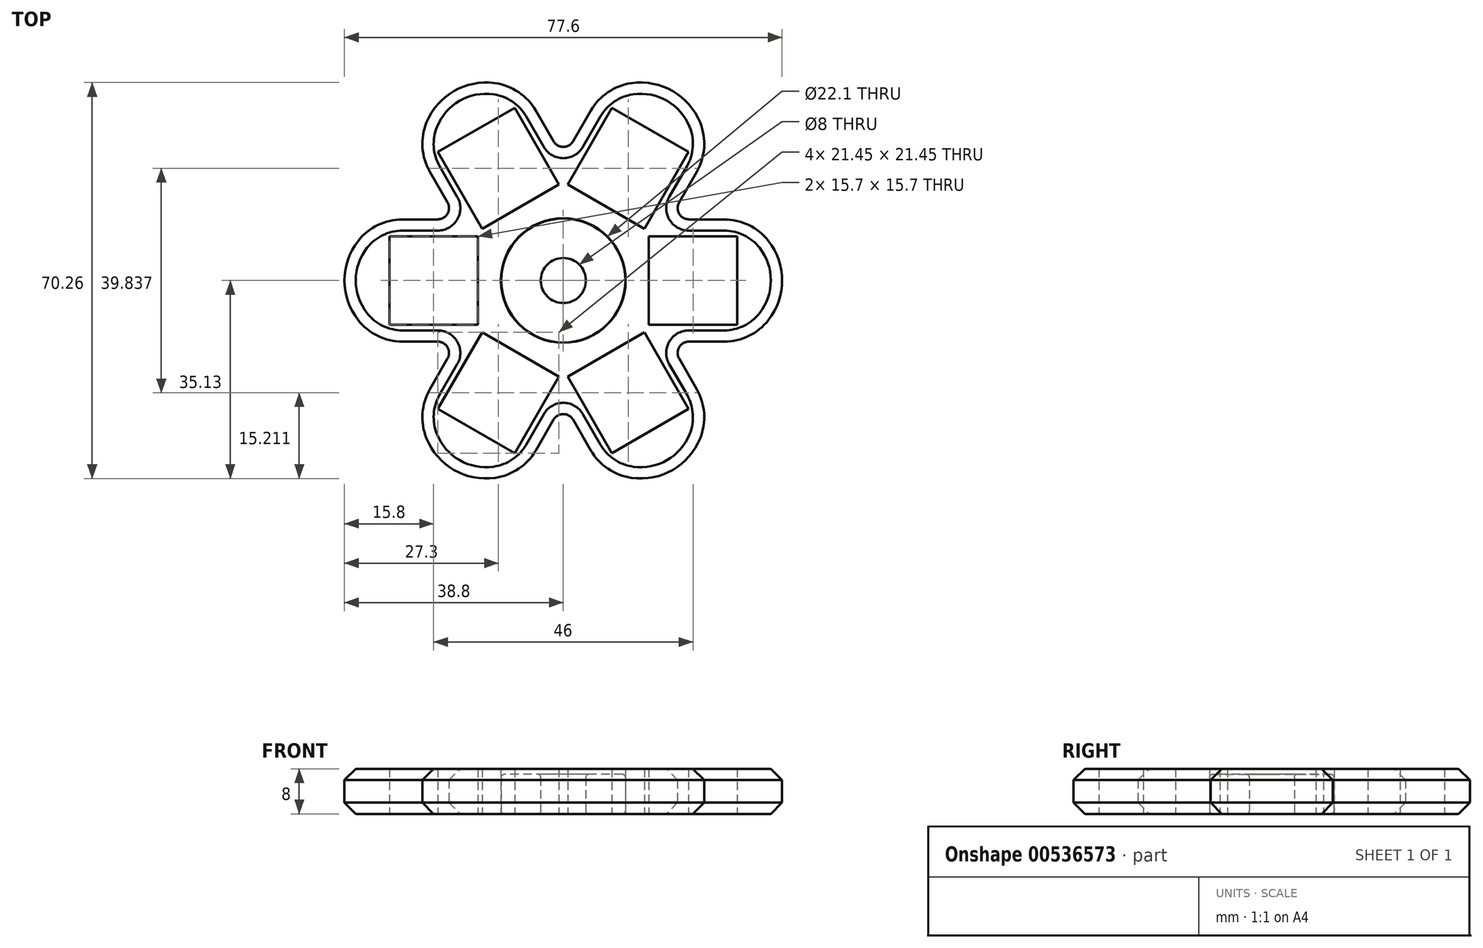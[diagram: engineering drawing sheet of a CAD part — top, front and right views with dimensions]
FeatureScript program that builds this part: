
annotation { "Feature Type Name" : "Feature", "Feature Type Description" : "" }
export const myFeature = defineFeature(function(context is Context, id is Id, definition is map)
    precondition{}
    {
        {
            var Q0;
            Q0=qCreatedBy(makeId("Top.planeOp"),FACE);
            var sketch = newSketch(context, id + "F0", { "sketchPlane" : qUnion([Q0])});
            skCircle(sketch, "E0", {"center": v(0, 0) * mm, "radius": 11 * mm});
            skCircle(sketch, "E1", {"center": v(0, 0) * mm, "radius": 4 * mm});
            skSolve(sketch);
        }
        {
            var Q0;
            Q0=makeQuery(id+"F0.imprint","IMPRINT",FACE,{"disambiguationData":[TD([[makeQuery(id+"F0.imprint","IMPRINT",EDGE,{"derivedFrom":sQuery(id+"F0.wireOp",EDGE,"E0")}),1.0]])]});
            extrude(context, id + "F1", {"entities" : qUnion([Q0]), "depth" : 7 * mm, "offsetDistance" : 25 * mm});
        }
        {
            var Q0;
            Q0=makeQuery(id+"F1.opExtrude","CAP_FACE",FACE,{"disambiguationData":[OSD([sQuery(id+"F0.wireOp",EDGE,"E0"),sQuery(id+"F0.wireOp",EDGE,"E1")])],"isStart":true});
            var sketch = newSketch(context, id + "F2", { "sketchPlane" : qUnion([Q0])});
            skCircle(sketch, "E2.0", {"center": v(0, 0) * mm, "radius": 11.05 * mm});
            skCircle(sketch, "E3.0", {"center": v(0, 0) * mm, "radius": 15.05 * mm});
            skLineSegment(sketch, "E4", {"start": v(0, 0) * mm, "end": v(-23, 0) * mm, "construction": true});
            skLineSegment(sketch, "E5.bottom", {"start": v(-30.85, -7.85) * mm, "end": v(-15.15, -7.85) * mm});
            skLineSegment(sketch, "E5.top", {"start": v(-30.85, 7.85) * mm, "end": v(-15.15, 7.85) * mm});
            skLineSegment(sketch, "E5.left", {"start": v(-30.85, -7.85) * mm, "end": v(-30.85, 7.85) * mm});
            skLineSegment(sketch, "E5.right", {"start": v(-15.15, -7.85) * mm, "end": v(-15.15, 7.85) * mm});
            skPoint(sketch, "E5.middle", {"position": v(-23, 0) * mm});
            skCircle(sketch, "E6", {"center": v(0, 0) * mm, "radius": 50 * mm, "construction": true});
            skLineSegment(sketch, "E7", {"start": v(-23, 0) * mm, "end": v(-38.8, 0) * mm, "construction": true});
            skLineSegment(sketch, "E8", {"start": v(-30.85, 7.85) * mm, "end": v(-30.85, 10.85) * mm, "construction": true});
            skLineSegment(sketch, "E9.0", {"start": v(-23, 10.85) * mm, "end": v(-30.85, 10.85) * mm});
            skLineSegment(sketch, "E9.1", {"start": v(0, 10.85) * mm, "end": v(-2.1, 10.85) * mm, "construction": true});
            skLineSegment(sketch, "E10.trimOffspring", {"start": v(-10.43, 10.85) * mm, "end": v(-23, 10.85) * mm});
            skLineSegment(sketch, "E11.MirrorCS", {"start": v(-10.43, -10.85) * mm, "end": v(-23, -10.85) * mm});
            skLineSegment(sketch, "E12.MirrorCS", {"start": v(-23, -10.85) * mm, "end": v(-30.85, -10.85) * mm});
            skArc(sketch, "E13", {"start": v(-30.85, 10.85) * mm, "mid": v(-38.8, 0) * mm, "end": v(-30.85, -10.85) * mm});
            skLineSegment(sketch, "E14.1.0", {"start": v(-8.63, -30.64) * mm, "end": v(-0.78, -17.05) * mm});
            skLineSegment(sketch, "E14.1.1", {"start": v(-0.78, -17.05) * mm, "end": v(-14.37, -9.2) * mm});
            skLineSegment(sketch, "E14.1.2", {"start": v(-22.22, -22.8) * mm, "end": v(-14.37, -9.2) * mm});
            skLineSegment(sketch, "E14.1.3", {"start": v(-14.61, -3.6) * mm, "end": v(-20.9, -14.5) * mm});
            skLineSegment(sketch, "E14.1.4", {"start": v(-20.9, -14.5) * mm, "end": v(-24.82, -21.3) * mm});
            skLineSegment(sketch, "E14.1.5", {"start": v(-8.63, -30.64) * mm, "end": v(-22.22, -22.8) * mm});
            skArc(sketch, "E14.1.6", {"start": v(-24.82, -21.3) * mm, "mid": v(-19.4, -33.6) * mm, "end": v(-6.03, -32.14) * mm});
            skLineSegment(sketch, "E14.1.7", {"start": v(-2.1, -25.34) * mm, "end": v(-6.03, -32.14) * mm});
            skLineSegment(sketch, "E14.1.8", {"start": v(4.18, -14.46) * mm, "end": v(-2.1, -25.34) * mm});
            skLineSegment(sketch, "E14.2.0", {"start": v(22.22, -22.8) * mm, "end": v(14.37, -9.2) * mm});
            skLineSegment(sketch, "E14.2.1", {"start": v(14.37, -9.2) * mm, "end": v(0.78, -17.05) * mm});
            skLineSegment(sketch, "E14.2.2", {"start": v(8.63, -30.64) * mm, "end": v(0.78, -17.05) * mm});
            skLineSegment(sketch, "E14.2.3", {"start": v(-4.18, -14.46) * mm, "end": v(2.1, -25.34) * mm});
            skLineSegment(sketch, "E14.2.4", {"start": v(2.1, -25.34) * mm, "end": v(6.03, -32.14) * mm});
            skLineSegment(sketch, "E14.2.5", {"start": v(22.22, -22.8) * mm, "end": v(8.63, -30.64) * mm});
            skArc(sketch, "E14.2.6", {"start": v(6.03, -32.14) * mm, "mid": v(19.4, -33.6) * mm, "end": v(24.82, -21.3) * mm});
            skLineSegment(sketch, "E14.2.7", {"start": v(20.9, -14.5) * mm, "end": v(24.82, -21.3) * mm});
            skLineSegment(sketch, "E14.2.8", {"start": v(14.61, -3.6) * mm, "end": v(20.9, -14.5) * mm});
            skCircle(sketch, "E15", {"center": v(0, 0) * mm, "radius": 32.7 * mm, "construction": true});
            skLineSegment(sketch, "E16.3.3.0", {"start": v(15.15, 7.85) * mm, "end": v(15.15, -7.85) * mm});
            skLineSegment(sketch, "E16.6.3.0", {"start": v(30.85, -7.85) * mm, "end": v(15.15, -7.85) * mm});
            skLineSegment(sketch, "E16.9.3.0", {"start": v(10.43, -10.85) * mm, "end": v(23, -10.85) * mm});
            skLineSegment(sketch, "E16.12.3.0", {"start": v(23, -10.85) * mm, "end": v(30.85, -10.85) * mm});
            skLineSegment(sketch, "E16.15.3.0", {"start": v(30.85, 7.85) * mm, "end": v(30.85, -7.85) * mm});
            skArc(sketch, "E16.18.3.0", {"start": v(30.85, -10.85) * mm, "mid": v(38.8, 0) * mm, "end": v(30.85, 10.85) * mm});
            skLineSegment(sketch, "E16.21.3.0", {"start": v(30.85, 7.85) * mm, "end": v(15.15, 7.85) * mm});
            skLineSegment(sketch, "E16.22.3.0", {"start": v(23, 10.85) * mm, "end": v(30.85, 10.85) * mm});
            skLineSegment(sketch, "E16.25.3.0", {"start": v(10.43, 10.85) * mm, "end": v(23, 10.85) * mm});
            skLineSegment(sketch, "E16.3.4.0", {"start": v(0.78, 17.05) * mm, "end": v(14.37, 9.2) * mm});
            skLineSegment(sketch, "E16.6.4.0", {"start": v(22.22, 22.8) * mm, "end": v(14.37, 9.2) * mm});
            skLineSegment(sketch, "E16.9.4.0", {"start": v(14.61, 3.6) * mm, "end": v(20.9, 14.5) * mm});
            skLineSegment(sketch, "E16.12.4.0", {"start": v(20.9, 14.5) * mm, "end": v(24.82, 21.3) * mm});
            skLineSegment(sketch, "E16.15.4.0", {"start": v(8.63, 30.64) * mm, "end": v(22.22, 22.8) * mm});
            skArc(sketch, "E16.18.4.0", {"start": v(24.82, 21.3) * mm, "mid": v(19.4, 33.6) * mm, "end": v(6.03, 32.14) * mm});
            skLineSegment(sketch, "E16.21.4.0", {"start": v(8.63, 30.64) * mm, "end": v(0.78, 17.05) * mm});
            skLineSegment(sketch, "E16.22.4.0", {"start": v(2.1, 25.34) * mm, "end": v(6.03, 32.14) * mm});
            skLineSegment(sketch, "E16.25.4.0", {"start": v(-4.18, 14.46) * mm, "end": v(2.1, 25.34) * mm});
            skLineSegment(sketch, "E16.3.5.0", {"start": v(-14.37, 9.2) * mm, "end": v(-0.78, 17.05) * mm});
            skLineSegment(sketch, "E16.6.5.0", {"start": v(-8.63, 30.64) * mm, "end": v(-0.78, 17.05) * mm});
            skLineSegment(sketch, "E16.9.5.0", {"start": v(4.18, 14.46) * mm, "end": v(-2.1, 25.34) * mm});
            skLineSegment(sketch, "E16.12.5.0", {"start": v(-2.1, 25.34) * mm, "end": v(-6.03, 32.14) * mm});
            skLineSegment(sketch, "E16.15.5.0", {"start": v(-22.22, 22.8) * mm, "end": v(-8.63, 30.64) * mm});
            skArc(sketch, "E16.18.5.0", {"start": v(-6.03, 32.14) * mm, "mid": v(-19.4, 33.6) * mm, "end": v(-24.82, 21.3) * mm});
            skLineSegment(sketch, "E16.21.5.0", {"start": v(-22.22, 22.8) * mm, "end": v(-14.37, 9.2) * mm});
            skLineSegment(sketch, "E16.22.5.0", {"start": v(-20.9, 14.5) * mm, "end": v(-24.82, 21.3) * mm});
            skLineSegment(sketch, "E16.25.5.0", {"start": v(-14.61, 3.6) * mm, "end": v(-20.9, 14.5) * mm});
            skSolve(sketch);
        }
        {
            var Q0;
            {var subQ5=sQuery(id+"F2.wireOp",EDGE,"E14.2.0");Q0=makeQuery(id+"F2.imprint","IMPRINT",FACE,{"disambiguationData":[TD([[makeQuery(id+"F2.imprint","IMPRINT",EDGE,{"derivedFrom":subQ5}),-1.0]])]});}
            var Q1;
            Q1=makeQuery(id+"F2.imprint","IMPRINT",FACE,{"disambiguationData":[TD([[makeQuery(id+"F2.imprint","IMPRINT",EDGE,{"derivedFrom":sQuery(id+"F2.wireOp",EDGE,"E2.0")}),-1.0]])]});
            var Q2;
            {var subQ6=sQuery(id+"F2.wireOp",EDGE,"E14.1.0");Q2=makeQuery(id+"F2.imprint","IMPRINT",FACE,{"disambiguationData":[TD([[makeQuery(id+"F2.imprint","IMPRINT",EDGE,{"derivedFrom":subQ6}),-1.0]])]});}
            var Q3;
            {var subQ5=sQuery(id+"F2.wireOp",EDGE,"E5.bottom");Q3=makeQuery(id+"F2.imprint","IMPRINT",FACE,{"disambiguationData":[TD([[makeQuery(id+"F2.imprint","IMPRINT",EDGE,{"derivedFrom":subQ5}),-1.0]])]});}
            var Q4;
            {var subQ0=sQuery(id+"F2.wireOp",EDGE,"E16.12.3.0");Q4=makeQuery(id+"F2.imprint","IMPRINT",FACE,{"disambiguationData":[TD([[makeQuery(id+"F2.imprint","IMPRINT",EDGE,{"derivedFrom":subQ0}),1.0]])]});}
            var Q5;
            {var subQ0=sQuery(id+"F2.wireOp",EDGE,"E16.12.4.0");Q5=makeQuery(id+"F2.imprint","IMPRINT",FACE,{"disambiguationData":[TD([[makeQuery(id+"F2.imprint","IMPRINT",EDGE,{"derivedFrom":subQ0}),1.0]])]});}
            var Q6;
            {var subQ1=sQuery(id+"F2.wireOp",EDGE,"E16.3.3.0");var subQ9=sQuery(id+"F2.wireOp",EDGE,"E3.0");var subQ10=makeQuery(id+"F2.imprint","INTERSECT",VERTEX,{"disambiguationData":[OD(0.0)],"derivedFrom":[subQ9,subQ1]});Q6=makeQuery(id+"F2.imprint","IMPRINT",FACE,{"disambiguationData":[TD([[makeQuery(id+"F2.imprint","IMPRINT",EDGE,{"disambiguationData":[TD([[subQ10,-1.0]])],"derivedFrom":subQ9}),-1.0]])]});}
            var Q7;
            {var subQ0=sQuery(id+"F2.wireOp",EDGE,"E14.2.4");Q7=makeQuery(id+"F2.imprint","IMPRINT",FACE,{"disambiguationData":[TD([[makeQuery(id+"F2.imprint","IMPRINT",EDGE,{"derivedFrom":subQ0}),1.0]])]});}
            var Q8;
            {var subQ0=sQuery(id+"F2.wireOp",EDGE,"E14.1.4");Q8=makeQuery(id+"F2.imprint","IMPRINT",FACE,{"disambiguationData":[TD([[makeQuery(id+"F2.imprint","IMPRINT",EDGE,{"derivedFrom":subQ0}),1.0]])]});}
            var Q9;
            {var subQ1=sQuery(id+"F2.wireOp",EDGE,"E5.left");Q9=makeQuery(id+"F2.imprint","IMPRINT",FACE,{"disambiguationData":[TD([[makeQuery(id+"F2.imprint","IMPRINT",EDGE,{"derivedFrom":subQ1}),1.0]])]});}
            var Q10;
            {var subQ0=sQuery(id+"F2.wireOp",EDGE,"E16.12.5.0");Q10=makeQuery(id+"F2.imprint","IMPRINT",FACE,{"disambiguationData":[TD([[makeQuery(id+"F2.imprint","IMPRINT",EDGE,{"derivedFrom":subQ0}),1.0]])]});}
            var Q11;
            {var subQ3=sQuery(id+"F2.wireOp",EDGE,"E3.0");var subQ5=sQuery(id+"F2.wireOp",EDGE,"E16.3.5.0");var subQ6=makeQuery(id+"F2.imprint","INTERSECT",VERTEX,{"disambiguationData":[OD(1.0)],"derivedFrom":[subQ3,subQ5]});Q11=makeQuery(id+"F2.imprint","IMPRINT",FACE,{"disambiguationData":[TD([[makeQuery(id+"F2.imprint","IMPRINT",EDGE,{"disambiguationData":[TD([[subQ6,-1.0]])],"derivedFrom":subQ3}),-1.0]])]});}
            var Q12;
            {var subQ1=sQuery(id+"F2.wireOp",EDGE,"E16.3.4.0");var subQ5=sQuery(id+"F2.wireOp",EDGE,"E3.0");var subQ6=makeQuery(id+"F2.imprint","INTERSECT",VERTEX,{"disambiguationData":[OD(1.0)],"derivedFrom":[subQ5,subQ1]});Q12=makeQuery(id+"F2.imprint","IMPRINT",FACE,{"disambiguationData":[TD([[makeQuery(id+"F2.imprint","IMPRINT",EDGE,{"disambiguationData":[TD([[subQ6,-1.0]])],"derivedFrom":subQ5}),-1.0]])]});}
            var Q13;
            {var subQ5=sQuery(id+"F2.wireOp",EDGE,"E16.25.4.0");var subQ6=sQuery(id+"F2.wireOp",EDGE,"E3.0");var subQ7=makeQuery(id+"F2.imprint","INTERSECT",VERTEX,{"derivedFrom":[subQ6,subQ5]});Q13=makeQuery(id+"F2.imprint","IMPRINT",FACE,{"disambiguationData":[TD([[makeQuery(id+"F2.imprint","IMPRINT",EDGE,{"disambiguationData":[TD([[subQ7,1.0]])],"derivedFrom":subQ6}),-1.0]])]});}
            var Q14;
            {var subQ5=sQuery(id+"F2.wireOp",EDGE,"E3.0");var subQ8=sQuery(id+"F2.wireOp",EDGE,"E16.25.3.0");var subQ9=makeQuery(id+"F2.imprint","INTERSECT",VERTEX,{"derivedFrom":[subQ5,subQ8]});Q14=makeQuery(id+"F2.imprint","IMPRINT",FACE,{"disambiguationData":[TD([[makeQuery(id+"F2.imprint","IMPRINT",EDGE,{"disambiguationData":[TD([[subQ9,1.0]])],"derivedFrom":subQ5}),-1.0]])]});}
            var Q15;
            {var subQ0=sQuery(id+"F2.wireOp",EDGE,"E10.trimOffspring");var subQ1=sQuery(id+"F2.wireOp",EDGE,"E3.0");var subQ2=makeQuery(id+"F2.imprint","INTERSECT",VERTEX,{"derivedFrom":[subQ1,subQ0]});Q15=makeQuery(id+"F2.imprint","IMPRINT",FACE,{"disambiguationData":[TD([[makeQuery(id+"F2.imprint","IMPRINT",EDGE,{"disambiguationData":[TD([[subQ2,-1.0]])],"derivedFrom":subQ1}),-1.0]])]});}
            var Q16;
            {var subQ0=sQuery(id+"F2.wireOp",EDGE,"E16.25.4.0");var subQ1=sQuery(id+"F2.wireOp",EDGE,"E3.0");var subQ2=makeQuery(id+"F2.imprint","INTERSECT",VERTEX,{"derivedFrom":[subQ1,subQ0]});Q16=makeQuery(id+"F2.imprint","IMPRINT",FACE,{"disambiguationData":[TD([[makeQuery(id+"F2.imprint","IMPRINT",EDGE,{"disambiguationData":[TD([[subQ2,-1.0]])],"derivedFrom":subQ1}),-1.0]])]});}
            var Q17;
            {var subQ0=sQuery(id+"F2.wireOp",EDGE,"E16.25.3.0");var subQ1=sQuery(id+"F2.wireOp",EDGE,"E3.0");var subQ2=makeQuery(id+"F2.imprint","INTERSECT",VERTEX,{"derivedFrom":[subQ1,subQ0]});Q17=makeQuery(id+"F2.imprint","IMPRINT",FACE,{"disambiguationData":[TD([[makeQuery(id+"F2.imprint","IMPRINT",EDGE,{"disambiguationData":[TD([[subQ2,-1.0]])],"derivedFrom":subQ1}),-1.0]])]});}
            var Q18;
            {var subQ0=sQuery(id+"F2.wireOp",EDGE,"E14.2.8");var subQ1=sQuery(id+"F2.wireOp",EDGE,"E3.0");var subQ2=makeQuery(id+"F2.imprint","INTERSECT",VERTEX,{"derivedFrom":[subQ1,subQ0]});Q18=makeQuery(id+"F2.imprint","IMPRINT",FACE,{"disambiguationData":[TD([[makeQuery(id+"F2.imprint","IMPRINT",EDGE,{"disambiguationData":[TD([[subQ2,-1.0]])],"derivedFrom":subQ1}),-1.0]])]});}
            var Q19;
            {var subQ0=sQuery(id+"F2.wireOp",EDGE,"E16.9.3.0");var subQ1=sQuery(id+"F2.wireOp",EDGE,"E3.0");var subQ2=makeQuery(id+"F2.imprint","INTERSECT",VERTEX,{"derivedFrom":[subQ1,subQ0]});Q19=makeQuery(id+"F2.imprint","IMPRINT",FACE,{"disambiguationData":[TD([[makeQuery(id+"F2.imprint","IMPRINT",EDGE,{"disambiguationData":[TD([[subQ2,1.0]])],"derivedFrom":subQ1}),-1.0]])]});}
            var Q20;
            {var subQ0=sQuery(id+"F2.wireOp",EDGE,"E14.1.8");var subQ1=sQuery(id+"F2.wireOp",EDGE,"E3.0");var subQ2=makeQuery(id+"F2.imprint","INTERSECT",VERTEX,{"derivedFrom":[subQ1,subQ0]});Q20=makeQuery(id+"F2.imprint","IMPRINT",FACE,{"disambiguationData":[TD([[makeQuery(id+"F2.imprint","IMPRINT",EDGE,{"disambiguationData":[TD([[subQ2,-1.0]])],"derivedFrom":subQ1}),-1.0]])]});}
            var Q21;
            {var subQ0=sQuery(id+"F2.wireOp",EDGE,"E14.2.3");var subQ1=sQuery(id+"F2.wireOp",EDGE,"E3.0");var subQ2=makeQuery(id+"F2.imprint","INTERSECT",VERTEX,{"derivedFrom":[subQ1,subQ0]});Q21=makeQuery(id+"F2.imprint","IMPRINT",FACE,{"disambiguationData":[TD([[makeQuery(id+"F2.imprint","IMPRINT",EDGE,{"disambiguationData":[TD([[subQ2,1.0]])],"derivedFrom":subQ1}),-1.0]])]});}
            var Q22;
            {var subQ0=sQuery(id+"F2.wireOp",EDGE,"E11.MirrorCS");var subQ1=sQuery(id+"F2.wireOp",EDGE,"E3.0");var subQ2=makeQuery(id+"F2.imprint","INTERSECT",VERTEX,{"derivedFrom":[subQ1,subQ0]});Q22=makeQuery(id+"F2.imprint","IMPRINT",FACE,{"disambiguationData":[TD([[makeQuery(id+"F2.imprint","IMPRINT",EDGE,{"disambiguationData":[TD([[subQ2,-1.0]])],"derivedFrom":subQ1}),-1.0]])]});}
            var Q23;
            {var subQ0=sQuery(id+"F2.wireOp",EDGE,"E14.1.3");var subQ1=sQuery(id+"F2.wireOp",EDGE,"E3.0");var subQ2=makeQuery(id+"F2.imprint","INTERSECT",VERTEX,{"derivedFrom":[subQ1,subQ0]});Q23=makeQuery(id+"F2.imprint","IMPRINT",FACE,{"disambiguationData":[TD([[makeQuery(id+"F2.imprint","IMPRINT",EDGE,{"disambiguationData":[TD([[subQ2,1.0]])],"derivedFrom":subQ1}),-1.0]])]});}
            var Q24;
            {var subQ0=sQuery(id+"F2.wireOp",EDGE,"E16.25.5.0");var subQ1=sQuery(id+"F2.wireOp",EDGE,"E3.0");var subQ2=makeQuery(id+"F2.imprint","INTERSECT",VERTEX,{"derivedFrom":[subQ1,subQ0]});Q24=makeQuery(id+"F2.imprint","IMPRINT",FACE,{"disambiguationData":[TD([[makeQuery(id+"F2.imprint","IMPRINT",EDGE,{"disambiguationData":[TD([[subQ2,-1.0]])],"derivedFrom":subQ1}),-1.0]])]});}
            extrude(context, id + "F3", {"entities" : qUnion([Q0, Q1, Q2, Q3, Q4, Q5, Q6, Q7, Q8, Q9, Q10, Q11, Q12, Q13, Q14, Q15, Q16, Q17, Q18, Q19, Q20, Q21, Q22, Q23, Q24]), "oppositeDirection" : true, "depth" : 8 * mm, "offsetDistance" : 25 * mm});
        }
        {
            var Q0;
            Q0=makeQuery(id+"F3.opExtrude","SWEPT_EDGE",EDGE,{"disambiguationData":[OSD([sQuery(id+"F2.wireOp",EDGE,"E11.MirrorCS"),sQuery(id+"F2.wireOp",EDGE,"E14.1.3")])]});
            var Q1;
            Q1=makeQuery(id+"F3.opExtrude","SWEPT_EDGE",EDGE,{"disambiguationData":[OSD([sQuery(id+"F2.wireOp",EDGE,"E14.1.8"),sQuery(id+"F2.wireOp",EDGE,"E14.2.3")])]});
            var Q2;
            Q2=makeQuery(id+"F3.opExtrude","SWEPT_EDGE",EDGE,{"disambiguationData":[OSD([sQuery(id+"F2.wireOp",EDGE,"E14.2.8"),sQuery(id+"F2.wireOp",EDGE,"E16.9.3.0")])]});
            var Q3;
            Q3=makeQuery(id+"F3.opExtrude","SWEPT_EDGE",EDGE,{"disambiguationData":[OSD([sQuery(id+"F2.wireOp",EDGE,"E16.25.4.0"),sQuery(id+"F2.wireOp",EDGE,"E16.9.5.0")])]});
            var Q4;
            Q4=makeQuery(id+"F3.opExtrude","SWEPT_EDGE",EDGE,{"disambiguationData":[OSD([sQuery(id+"F2.wireOp",EDGE,"E10.trimOffspring"),sQuery(id+"F2.wireOp",EDGE,"E16.25.5.0")])]});
            var Q5;
            Q5=makeQuery(id+"F3.opExtrude","SWEPT_EDGE",EDGE,{"disambiguationData":[OSD([sQuery(id+"F2.wireOp",EDGE,"E16.25.3.0"),sQuery(id+"F2.wireOp",EDGE,"E16.9.4.0")])]});
            fillet(context, id + "F4", {"entities" : qUnion([Q0, Q1, Q2, Q3, Q4, Q5]), "radius" : 2 * mm, "tangentPropagation" : true, "allowEdgeOverflow" : false});
        }
        {
            var Q0;
            Q0=makeQuery(id+"F3.opExtrude","SWEPT_EDGE",EDGE,{"disambiguationData":[OSD([sQuery(id+"F2.wireOp",EDGE,"E16.12.4.0"),sQuery(id+"F2.wireOp",EDGE,"E16.18.4.0")])]});
            var Q1;
            Q1=makeQuery(id+"F3.opExtrude","SWEPT_EDGE",EDGE,{"disambiguationData":[OSD([sQuery(id+"F2.wireOp",EDGE,"E16.18.3.0"),sQuery(id+"F2.wireOp",EDGE,"E16.22.3.0")])]});
            var Q2;
            Q2=makeQuery(id+"F3.opExtrude","SWEPT_EDGE",EDGE,{"disambiguationData":[OSD([sQuery(id+"F2.wireOp",EDGE,"E16.12.3.0"),sQuery(id+"F2.wireOp",EDGE,"E16.18.3.0")])]});
            var Q3;
            Q3=makeQuery(id+"F3.opExtrude","SWEPT_EDGE",EDGE,{"disambiguationData":[OSD([sQuery(id+"F2.wireOp",EDGE,"E14.2.6"),sQuery(id+"F2.wireOp",EDGE,"E14.2.7")])]});
            var Q4;
            Q4=makeQuery(id+"F3.opExtrude","SWEPT_EDGE",EDGE,{"disambiguationData":[OSD([sQuery(id+"F2.wireOp",EDGE,"E14.2.4"),sQuery(id+"F2.wireOp",EDGE,"E14.2.6")])]});
            var Q5;
            Q5=makeQuery(id+"F3.opExtrude","SWEPT_EDGE",EDGE,{"disambiguationData":[OSD([sQuery(id+"F2.wireOp",EDGE,"E14.1.6"),sQuery(id+"F2.wireOp",EDGE,"E14.1.7")])]});
            var Q6;
            Q6=makeQuery(id+"F3.opExtrude","SWEPT_EDGE",EDGE,{"disambiguationData":[OSD([sQuery(id+"F2.wireOp",EDGE,"E14.1.4"),sQuery(id+"F2.wireOp",EDGE,"E14.1.6")])]});
            var Q7;
            Q7=makeQuery(id+"F3.opExtrude","SWEPT_EDGE",EDGE,{"disambiguationData":[OSD([sQuery(id+"F2.wireOp",EDGE,"E12.MirrorCS"),sQuery(id+"F2.wireOp",EDGE,"E13")])]});
            var Q8;
            Q8=makeQuery(id+"F3.opExtrude","SWEPT_EDGE",EDGE,{"disambiguationData":[OSD([sQuery(id+"F2.wireOp",EDGE,"E9.0"),sQuery(id+"F2.wireOp",EDGE,"E13")])]});
            var Q9;
            Q9=makeQuery(id+"F3.opExtrude","SWEPT_EDGE",EDGE,{"disambiguationData":[OSD([sQuery(id+"F2.wireOp",EDGE,"E16.18.5.0"),sQuery(id+"F2.wireOp",EDGE,"E16.22.5.0")])]});
            var Q10;
            Q10=makeQuery(id+"F3.opExtrude","SWEPT_EDGE",EDGE,{"disambiguationData":[OSD([sQuery(id+"F2.wireOp",EDGE,"E16.12.5.0"),sQuery(id+"F2.wireOp",EDGE,"E16.18.5.0")])]});
            var Q11;
            Q11=makeQuery(id+"F3.opExtrude","SWEPT_EDGE",EDGE,{"disambiguationData":[OSD([sQuery(id+"F2.wireOp",EDGE,"E16.18.4.0"),sQuery(id+"F2.wireOp",EDGE,"E16.22.4.0")])]});
            fillet(context, id + "F5", {"entities" : qUnion([Q0, Q1, Q2, Q3, Q4, Q5, Q6, Q7, Q8, Q9, Q10, Q11]), "radius" : 10 * mm, "tangentPropagation" : true, "allowEdgeOverflow" : false});
        }
        {
            var Q0;
            Q0=makeQuery(id+"F3.opExtrude","CAP_EDGE",EDGE,{"disambiguationData":[OSD([sQuery(id+"F2.wireOp",EDGE,"E14.2.6")])],"isStart":false});
            var Q1;
            Q1=makeQuery(id+"F3.opExtrude","CAP_EDGE",EDGE,{"disambiguationData":[OSD([sQuery(id+"F2.wireOp",EDGE,"E14.1.6")])],"isStart":false});
            var Q2;
            {var subQ0=sQuery(id+"F2.wireOp",EDGE,"E13");var subQ1=sQuery(id+"F2.wireOp",EDGE,"E9.0");Q2=makeQuery(id+"F5.opFillet","BLEND_EDGE",EDGE,{"blendedFrom":[makeQuery(id+"F3.opExtrude","SWEPT_EDGE",EDGE,{"disambiguationData":[OSD([subQ1,subQ0])]}),makeQuery(id+"F3.opExtrude","CAP_FACE",FACE,{"disambiguationData":[OSD([sQuery(id+"F2.wireOp",EDGE,"E2.0"),sQuery(id+"F2.wireOp",EDGE,"E3.0"),sQuery(id+"F2.wireOp",EDGE,"E5.bottom"),sQuery(id+"F2.wireOp",EDGE,"E5.top"),sQuery(id+"F2.wireOp",EDGE,"E5.left"),sQuery(id+"F2.wireOp",EDGE,"E5.right"),subQ1,sQuery(id+"F2.wireOp",EDGE,"E10.trimOffspring"),sQuery(id+"F2.wireOp",EDGE,"E11.MirrorCS"),sQuery(id+"F2.wireOp",EDGE,"E12.MirrorCS"),subQ0,sQuery(id+"F2.wireOp",EDGE,"E14.1.0"),sQuery(id+"F2.wireOp",EDGE,"E14.1.1"),sQuery(id+"F2.wireOp",EDGE,"E14.1.2"),sQuery(id+"F2.wireOp",EDGE,"E14.1.3"),sQuery(id+"F2.wireOp",EDGE,"E14.1.4"),sQuery(id+"F2.wireOp",EDGE,"E14.1.5"),sQuery(id+"F2.wireOp",EDGE,"E14.1.6"),sQuery(id+"F2.wireOp",EDGE,"E14.1.7"),sQuery(id+"F2.wireOp",EDGE,"E14.1.8"),sQuery(id+"F2.wireOp",EDGE,"E14.2.0"),sQuery(id+"F2.wireOp",EDGE,"E14.2.1"),sQuery(id+"F2.wireOp",EDGE,"E14.2.2"),sQuery(id+"F2.wireOp",EDGE,"E14.2.3"),sQuery(id+"F2.wireOp",EDGE,"E14.2.4"),sQuery(id+"F2.wireOp",EDGE,"E14.2.5"),sQuery(id+"F2.wireOp",EDGE,"E14.2.6"),sQuery(id+"F2.wireOp",EDGE,"E14.2.7"),sQuery(id+"F2.wireOp",EDGE,"E14.2.8")])],"isStart":false})],"blendedInto":[makeQuery(id+"F3.opExtrude","CAP_FACE",FACE,{"disambiguationData":[OSD([sQuery(id+"F2.wireOp",EDGE,"E2.0"),sQuery(id+"F2.wireOp",EDGE,"E3.0"),sQuery(id+"F2.wireOp",EDGE,"E5.bottom"),sQuery(id+"F2.wireOp",EDGE,"E5.top"),sQuery(id+"F2.wireOp",EDGE,"E5.left"),sQuery(id+"F2.wireOp",EDGE,"E5.right"),subQ1,sQuery(id+"F2.wireOp",EDGE,"E10.trimOffspring"),sQuery(id+"F2.wireOp",EDGE,"E11.MirrorCS"),sQuery(id+"F2.wireOp",EDGE,"E12.MirrorCS"),subQ0,sQuery(id+"F2.wireOp",EDGE,"E14.1.0"),sQuery(id+"F2.wireOp",EDGE,"E14.1.1"),sQuery(id+"F2.wireOp",EDGE,"E14.1.2"),sQuery(id+"F2.wireOp",EDGE,"E14.1.3"),sQuery(id+"F2.wireOp",EDGE,"E14.1.4"),sQuery(id+"F2.wireOp",EDGE,"E14.1.5"),sQuery(id+"F2.wireOp",EDGE,"E14.1.6"),sQuery(id+"F2.wireOp",EDGE,"E14.1.7"),sQuery(id+"F2.wireOp",EDGE,"E14.1.8"),sQuery(id+"F2.wireOp",EDGE,"E14.2.0"),sQuery(id+"F2.wireOp",EDGE,"E14.2.1"),sQuery(id+"F2.wireOp",EDGE,"E14.2.2"),sQuery(id+"F2.wireOp",EDGE,"E14.2.3"),sQuery(id+"F2.wireOp",EDGE,"E14.2.4"),sQuery(id+"F2.wireOp",EDGE,"E14.2.5"),sQuery(id+"F2.wireOp",EDGE,"E14.2.6"),sQuery(id+"F2.wireOp",EDGE,"E14.2.7"),sQuery(id+"F2.wireOp",EDGE,"E14.2.8")])],"isStart":false})]});}
            var Q3;
            Q3=makeQuery(id+"F3.opExtrude","CAP_EDGE",EDGE,{"disambiguationData":[OSD([sQuery(id+"F2.wireOp",EDGE,"E14.2.6")])],"isStart":true});
            var Q4;
            Q4=makeQuery(id+"F3.opExtrude","CAP_EDGE",EDGE,{"disambiguationData":[OSD([sQuery(id+"F2.wireOp",EDGE,"E13")])],"isStart":true});
            var Q5;
            Q5=makeQuery(id+"F3.opExtrude","CAP_EDGE",EDGE,{"disambiguationData":[OSD([sQuery(id+"F2.wireOp",EDGE,"E14.1.6")])],"isStart":true});
            chamfer(context, id + "F6", {"entities" : qUnion([Q0, Q1, Q2, Q3, Q4, Q5]), "width" : 2 * mm, "tangentPropagation" : true});
        }
        {
            var Q0;
            Q0=makeQuery(id+"F1.opExtrude","CAP_FACE",FACE,{"disambiguationData":[OSD([sQuery(id+"F0.wireOp",EDGE,"E0"),sQuery(id+"F0.wireOp",EDGE,"E1")])],"isStart":true});
            var Q1;
            Q1=makeQuery(id+"F1.opExtrude","CAP_FACE",FACE,{"disambiguationData":[OSD([sQuery(id+"F0.wireOp",EDGE,"E0"),sQuery(id+"F0.wireOp",EDGE,"E1")])],"isStart":false});
            fillet(context, id + "F7", {"entities" : qUnion([Q0, Q1]), "radius" : .5 * mm, "tangentPropagation" : true, "allowEdgeOverflow" : false});
        }
    });
